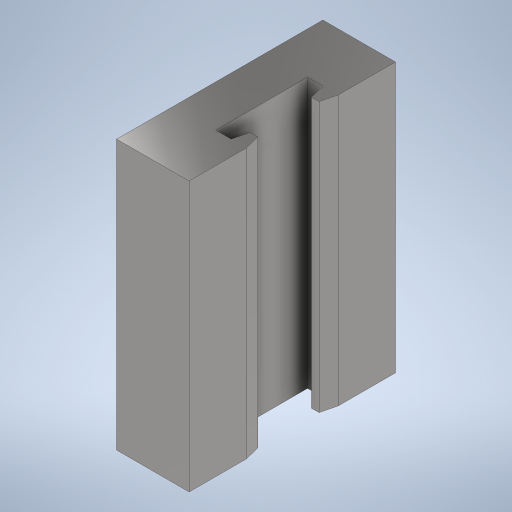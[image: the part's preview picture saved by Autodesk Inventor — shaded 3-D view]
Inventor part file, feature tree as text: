
AUTODESK INVENTOR PART (.ipt)
format: ipt  version: 2023 (Build 270158000, 158)  size: 252,928 bytes
history: native  units: mm
features: sketch x2, extrude x1, hole x1
ambient origin geometry x8: Origin, YZ Plane, XZ Plane, XY Plane, X Axis, Y Axis, Z Axis, Center Point
bodies: Solid1 (feature_tree)
feature tree (4):
  extrude  "Extrusion1"  Depth=9.5mm
  hole  "Hole1"  [1 undecoded]
  sketch  "Sketch1"  dims[d2=8.0mm d3=1.0mm d5=0.5mm d6=4.0mm d8=9.5mm]
  sketch  "Sketch2"  dims[d9=27.0mm d10=35.25mm d11=0.0mm d12=0.0mm d13=12.0mm d14=2.0mm d15=2.0mm d16=15.0mm d17=15.0mm d18=20.0mm d19=20.0mm d20=0.0mm d21=0.0mm d22=35.25mm d23=27.0mm d24=7.625mm d25=6.0mm d26=2.459mm d27=4.0mm d28=3.023mm d29=2.0mm d30=14.3117mm d31=5.0mm d32=20.594885mm]
note: 1 required parameter value undecoded (feature->parameter linkage not recoverable at this tier; creation-order binding heuristic only, values carry confidence <= 0.55)
